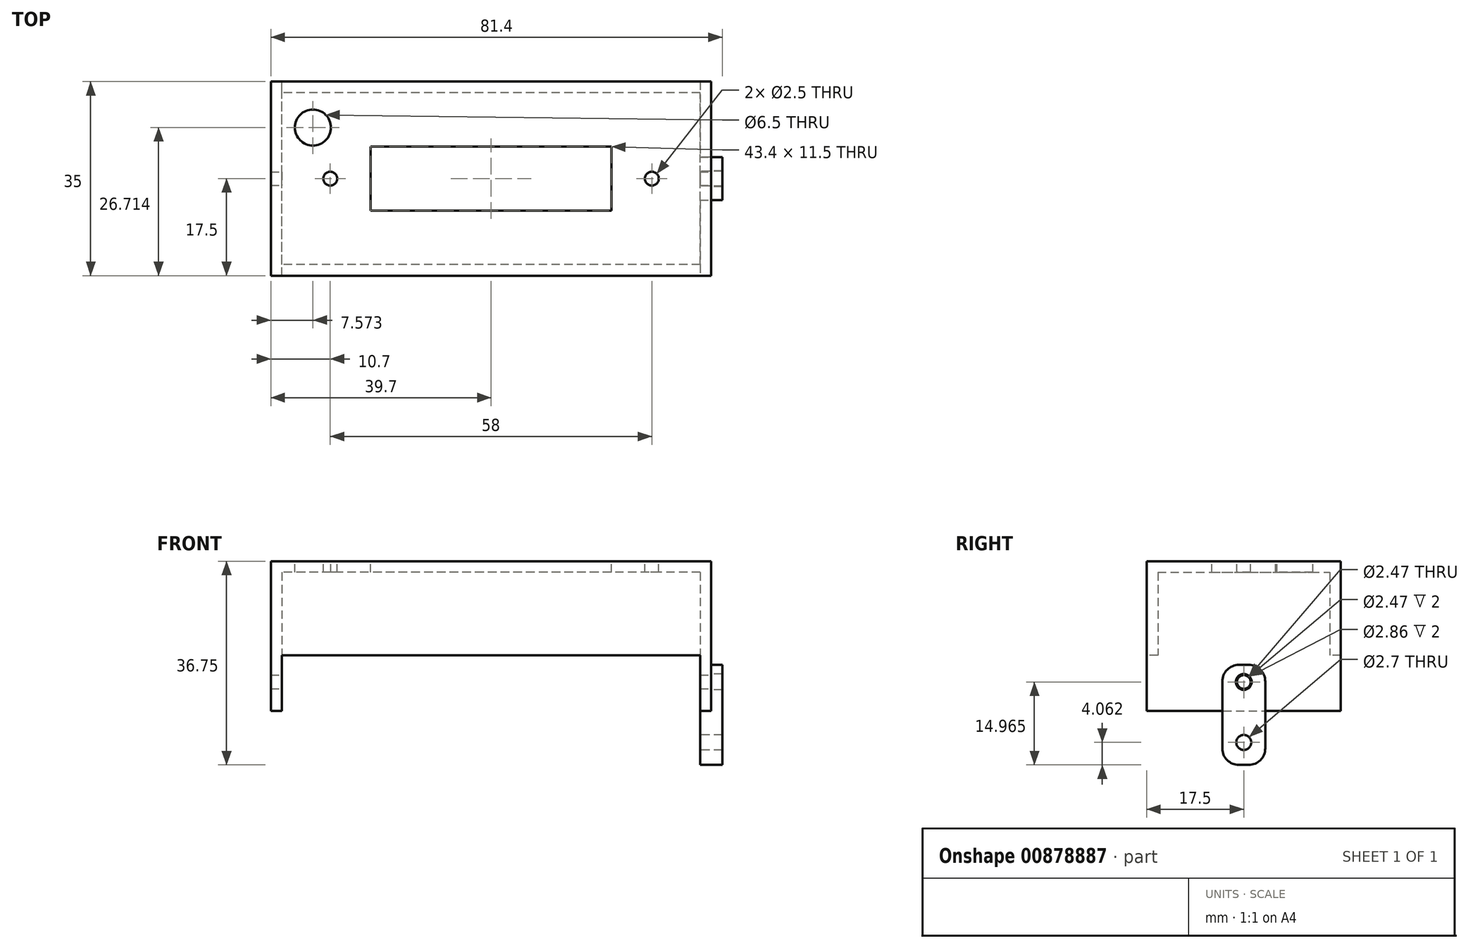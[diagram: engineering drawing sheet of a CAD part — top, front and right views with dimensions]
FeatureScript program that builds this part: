
annotation { "Feature Type Name" : "Feature", "Feature Type Description" : "" }
export const myFeature = defineFeature(function(context is Context, id is Id, definition is map)
    precondition{}
    {
        {
            var Q0;
            Q0=qCreatedBy(makeId("Top.planeOp"),FACE);
            var sketch = newSketch(context, id + "F0", { "sketchPlane" : qUnion([Q0])});
            skLineSegment(sketch, "E0.bottom", {"start": v(39.7, -17.5) * mm, "end": v(-39.7, -17.5) * mm});
            skLineSegment(sketch, "E0.top", {"start": v(39.7, 17.5) * mm, "end": v(-39.7, 17.5) * mm});
            skLineSegment(sketch, "E0.left", {"start": v(39.7, -17.5) * mm, "end": v(39.7, 17.5) * mm});
            skLineSegment(sketch, "E0.right", {"start": v(-39.7, -17.5) * mm, "end": v(-39.7, 17.5) * mm});
            skPoint(sketch, "E0.middle", {"position": v(0, 0) * mm});
            skSolve(sketch);
        }
        {
            var Q0;
            Q0=makeQuery(id+"F0.imprint","IMPRINT",FACE,{"disambiguationData":[TD([[makeQuery(id+"F0.imprint","IMPRINT",EDGE,{"derivedFrom":sQuery(id+"F0.wireOp",EDGE,"E0.bottom")}),-1.0]])]});
            extrude(context, id + "F1", {"entities" : qUnion([Q0]), "depth" : 17 * mm, "offsetDistance" : 25 * mm});
        }
        {
            var Q0;
            Q0=makeQuery(id+"F1.opExtrude","CAP_FACE",FACE,{"disambiguationData":[OSD([sQuery(id+"F0.wireOp",EDGE,"E0.bottom"),sQuery(id+"F0.wireOp",EDGE,"E0.top"),sQuery(id+"F0.wireOp",EDGE,"E0.left"),sQuery(id+"F0.wireOp",EDGE,"E0.right")])],"isStart":true});
            shell(context, id + "F2", {"entities" : qUnion([Q0]), "thickness" : 2 * mm});
        }
        {
            var Q0;
            Q0=makeQuery(id+"F1.opExtrude","CAP_FACE",FACE,{"disambiguationData":[OSD([sQuery(id+"F0.wireOp",EDGE,"E0.bottom"),sQuery(id+"F0.wireOp",EDGE,"E0.top"),sQuery(id+"F0.wireOp",EDGE,"E0.left"),sQuery(id+"F0.wireOp",EDGE,"E0.right")])],"isStart":true});
            var sketch = newSketch(context, id + "F3", { "sketchPlane" : qUnion([Q0])});
            skLineSegment(sketch, "E1.0", {"start": v(-37.7, 15.5) * mm, "end": v(-37.7, -15.5) * mm});
            skLineSegment(sketch, "E2.0", {"start": v(-39.7, 17.5) * mm, "end": v(-39.7, -17.5) * mm});
            skLineSegment(sketch, "E3.0", {"start": v(37.7, 15.5) * mm, "end": v(37.7, -15.5) * mm});
            skLineSegment(sketch, "E4.0", {"start": v(39.7, 17.5) * mm, "end": v(39.7, -17.5) * mm});
            skLineSegment(sketch, "E5", {"start": v(-37.7, 15.5) * mm, "end": v(-37.7, 17.5) * mm});
            skLineSegment(sketch, "E6", {"start": v(-37.7, 17.5) * mm, "end": v(-37.7, -15.5) * mm});
            skLineSegment(sketch, "E7", {"start": v(-37.7, -15.5) * mm, "end": v(-37.7, -17.5) * mm});
            skLineSegment(sketch, "E8", {"start": v(37.7, 15.5) * mm, "end": v(37.7, 17.5) * mm});
            skLineSegment(sketch, "E9", {"start": v(37.7, -15.5) * mm, "end": v(37.7, -17.5) * mm});
            skSolve(sketch);
        }
        {
            var Q0;
            Q0=makeQuery(id+"F3.imprint","IMPRINT",FACE,{"disambiguationData":[TD([[makeQuery(id+"F3.imprint","IMPRINT",EDGE,{"derivedFrom":sQuery(id+"F3.wireOp",EDGE,"E3.0")}),1.0]])]});
            var Q1;
            {var subQ8=sQuery(id+"F3.wireOp",EDGE,"E2.0");Q1=makeQuery(id+"F3.imprint","IMPRINT",FACE,{"disambiguationData":[TD([[makeQuery(id+"F3.imprint","IMPRINT",EDGE,{"derivedFrom":subQ8}),1.0]])]});}
            extrude(context, id + "F4", {"entities" : qUnion([Q0, Q1]), "operationType" : NewBodyOperationType.ADD, "depth" : 10 * mm, "offsetDistance" : 25 * mm});
        }
        {
            var Q0;
            Q0=makeQuery(id+"F1.opExtrude","CAP_FACE",FACE,{"disambiguationData":[OSD([sQuery(id+"F0.wireOp",EDGE,"E0.bottom"),sQuery(id+"F0.wireOp",EDGE,"E0.top"),sQuery(id+"F0.wireOp",EDGE,"E0.left"),sQuery(id+"F0.wireOp",EDGE,"E0.right")])],"isStart":false});
            var sketch = newSketch(context, id + "F5", { "sketchPlane" : qUnion([Q0])});
            skLineSegment(sketch, "E10.bottom", {"start": v(21.7, -5.75) * mm, "end": v(-21.7, -5.75) * mm});
            skLineSegment(sketch, "E10.top", {"start": v(21.7, 5.75) * mm, "end": v(-21.7, 5.75) * mm});
            skLineSegment(sketch, "E10.left", {"start": v(21.7, -5.75) * mm, "end": v(21.7, 5.75) * mm});
            skLineSegment(sketch, "E10.right", {"start": v(-21.7, -5.75) * mm, "end": v(-21.7, 5.75) * mm});
            skPoint(sketch, "E10.middle", {"position": v(0, 0) * mm});
            skCircle(sketch, "E11", {"center": v(-29, 0) * mm, "radius": 1.25 * mm});
            skCircle(sketch, "E12.MirrorC", {"center": v(29, 0) * mm, "radius": 1.25 * mm});
            skSolve(sketch);
        }
        {
            var Q0;
            Q0=makeQuery(id+"F4.boolean.opBoolean","MERGE",FACE,{"derivedFrom":[makeQuery(id+"F1.opExtrude","SWEPT_FACE",FACE,{"disambiguationData":[OSD([sQuery(id+"F0.wireOp",EDGE,"E0.left")])]}),makeQuery(id+"F4.opExtrude","SWEPT_FACE",FACE,{"disambiguationData":[OSD([sQuery(id+"F3.wireOp",EDGE,"E4.0")])]})]});
            var sketch = newSketch(context, id + "F6", { "sketchPlane" : qUnion([Q0])});
            skCircle(sketch, "E13", {"center": v(0, -4.78) * mm, "radius": 1.24 * mm});
            skSolve(sketch);
        }
        {
            var Q0;
            Q0=makeQuery(id+"F6.imprint","IMPRINT",FACE,{"disambiguationData":[TD([[makeQuery(id+"F6.imprint","IMPRINT",EDGE,{"derivedFrom":sQuery(id+"F6.wireOp",EDGE,"E13")}),1.0]])]});
            extrude(context, id + "F7", {"entities" : qUnion([Q0]), "operationType" : NewBodyOperationType.REMOVE, "endBound" : BoundingType.THROUGH_ALL, "oppositeDirection" : true, "depth" : 25 * mm, "offsetDistance" : 25 * mm});
        }
        {
            var Q0;
            Q0 = qSketchRegion(id + "F5", true);
            extrude(context, id + "F8", {"entities" : qUnion([Q0]), "operationType" : NewBodyOperationType.REMOVE, "oppositeDirection" : true, "depth" : 25 * mm, "offsetDistance" : 25 * mm});
        }
        {
            var Q0;
            Q0=makeQuery(id+"F1.opExtrude","CAP_FACE",FACE,{"disambiguationData":[OSD([sQuery(id+"F0.wireOp",EDGE,"E0.bottom"),sQuery(id+"F0.wireOp",EDGE,"E0.top"),sQuery(id+"F0.wireOp",EDGE,"E0.left"),sQuery(id+"F0.wireOp",EDGE,"E0.right")])],"isStart":false});
            var sketch = newSketch(context, id + "F9", { "sketchPlane" : qUnion([Q0])});
            skCircle(sketch, "E14", {"center": v(-32.13, 9.21) * mm, "radius": 3.25 * mm});
            skSolve(sketch);
        }
        {
            var Q0;
            Q0=makeQuery(id+"F9.imprint","IMPRINT",FACE,{"disambiguationData":[TD([[makeQuery(id+"F9.imprint","IMPRINT",EDGE,{"derivedFrom":sQuery(id+"F9.wireOp",EDGE,"E14")}),1.0]])]});
            extrude(context, id + "F10", {"entities" : qUnion([Q0]), "operationType" : NewBodyOperationType.REMOVE, "oppositeDirection" : true, "depth" : 25 * mm, "offsetDistance" : 25 * mm});
        }
        {
            var Q0;
            Q0=makeQuery(id+"F4.boolean.opBoolean","MERGE",FACE,{"derivedFrom":[makeQuery(id+"F1.opExtrude","SWEPT_FACE",FACE,{"disambiguationData":[OSD([sQuery(id+"F0.wireOp",EDGE,"E0.left")])]}),makeQuery(id+"F4.opExtrude","SWEPT_FACE",FACE,{"disambiguationData":[OSD([sQuery(id+"F3.wireOp",EDGE,"E4.0")])]})]});
            var sketch = newSketch(context, id + "F11", { "sketchPlane" : qUnion([Q0])});
            skCircle(sketch, "E15", {"center": v(0, -4.78) * mm, "radius": 1.43 * mm});
            skCircle(sketch, "E16", {"center": v(0, -15.69) * mm, "radius": 1.35 * mm});
            skLineSegment(sketch, "E17.bottom", {"start": v(0.87, -19.75) * mm, "end": v(-0.87, -19.75) * mm});
            skLineSegment(sketch, "E17.top", {"start": v(0.87, -1.7) * mm, "end": v(-0.87, -1.7) * mm});
            skLineSegment(sketch, "E17.left", {"start": v(3.87, -16.75) * mm, "end": v(3.87, -4.7) * mm});
            skLineSegment(sketch, "E17.right", {"start": v(-3.87, -16.75) * mm, "end": v(-3.87, -4.7) * mm});
            skPoint(sketch, "E17.middle", {"position": v(0, -10.73) * mm});
            skPoint(sketch, "E18.visualSharp", {"position": v(-3.87, -1.7) * mm});
            skArc(sketch, "E18.filletArc", {"start": v(-0.87, -1.7) * mm, "mid": v(-3, -2.59) * mm, "end": v(-3.87, -4.7) * mm});
            skPoint(sketch, "E19.visualSharp", {"position": v(3.87, -1.7) * mm});
            skArc(sketch, "E19.filletArc", {"start": v(3.87, -4.7) * mm, "mid": v(3, -2.59) * mm, "end": v(0.87, -1.7) * mm});
            skPoint(sketch, "E20.visualSharp", {"position": v(-3.87, -19.75) * mm});
            skArc(sketch, "E20.filletArc", {"start": v(-3.87, -16.75) * mm, "mid": v(-3, -18.87) * mm, "end": v(-0.87, -19.75) * mm});
            skPoint(sketch, "E21.visualSharp", {"position": v(3.87, -19.75) * mm});
            skArc(sketch, "E21.filletArc", {"start": v(0.87, -19.75) * mm, "mid": v(3, -18.87) * mm, "end": v(3.87, -16.75) * mm});
            skSolve(sketch);
        }
        {
            var Q0;
            Q0=makeQuery(id+"F11.imprint","IMPRINT",FACE,{"disambiguationData":[TD([[makeQuery(id+"F11.imprint","IMPRINT",EDGE,{"derivedFrom":sQuery(id+"F11.wireOp",EDGE,"E15")}),-1.0]])]});
            var Q1;
            Q1=makeQuery(id+"F11.imprint","IMPRINT",FACE,{"disambiguationData":[TD([[makeQuery(id+"F11.imprint","IMPRINT",EDGE,{"derivedFrom":sQuery(id+"F11.wireOp",EDGE,"E16")}),-1.0]])]});
            extrude(context, id + "F12", {"entities" : qUnion([Q0, Q1]), "depth" : 2 * mm, "offsetDistance" : 25 * mm});
        }
        {
            var Q0;
            Q0=makeQuery(id+"F11.imprint","IMPRINT",FACE,{"disambiguationData":[TD([[makeQuery(id+"F11.imprint","IMPRINT",EDGE,{"derivedFrom":sQuery(id+"F11.wireOp",EDGE,"E16")}),-1.0]])]});
            extrude(context, id + "F13", {"entities" : qUnion([Q0]), "operationType" : NewBodyOperationType.ADD, "oppositeDirection" : true, "depth" : 2 * mm, "offsetDistance" : 25 * mm});
        }
    });
